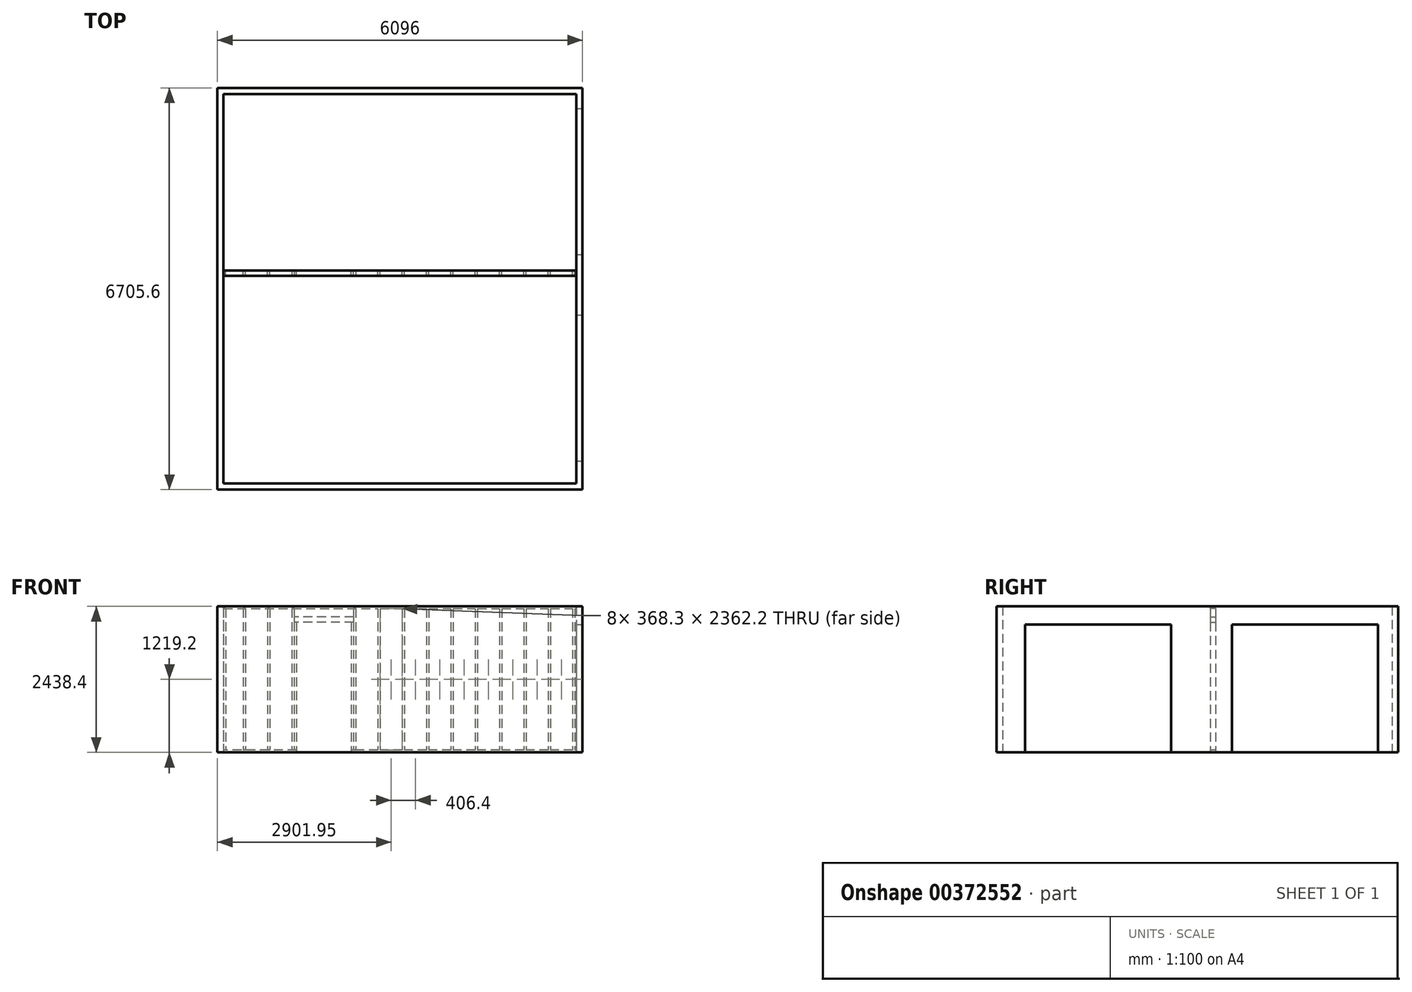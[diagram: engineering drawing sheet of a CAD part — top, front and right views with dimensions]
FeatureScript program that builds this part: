
annotation { "Feature Type Name" : "Feature", "Feature Type Description" : "" }
export const myFeature = defineFeature(function(context is Context, id is Id, definition is map)
    precondition{}
    {
        {
            var Q0;
            Q0=qCreatedBy(makeId("Top.planeOp"),FACE);
            var sketch = newSketch(context, id + "F0", { "sketchPlane" : qUnion([Q0])});
            skLineSegment(sketch, "E0.bottom", {"start": v(-222.03, 6557.87) * mm, "end": v(5873.97, 6557.87) * mm});
            skLineSegment(sketch, "E0.top", {"start": v(-222.03, -147.73) * mm, "end": v(5873.97, -147.73) * mm});
            skLineSegment(sketch, "E0.left", {"start": v(-222.03, 6557.87) * mm, "end": v(-222.03, -147.73) * mm});
            skLineSegment(sketch, "E0.right", {"start": v(5873.97, 6557.87) * mm, "end": v(5873.97, -147.73) * mm});
            skLineSegment(sketch, "E1.bottom", {"start": v(-120.43, 6456.27) * mm, "end": v(5772.37, 6456.27) * mm});
            skLineSegment(sketch, "E1.top", {"start": v(-120.43, -46.13) * mm, "end": v(5772.37, -46.13) * mm});
            skLineSegment(sketch, "E1.left", {"start": v(-120.43, 6456.27) * mm, "end": v(-120.43, -46.13) * mm});
            skLineSegment(sketch, "E1.right", {"start": v(5772.37, 6456.27) * mm, "end": v(5772.37, -46.13) * mm});
            skSolve(sketch);
        }
        {
            var Q0;
            Q0=makeQuery(id+"F0.imprint","IMPRINT",FACE,{"disambiguationData":[TD([[makeQuery(id+"F0.imprint","IMPRINT",EDGE,{"derivedFrom":sQuery(id+"F0.wireOp",EDGE,"E0.bottom")}),-1.0]])]});
            extrude(context, id + "F1", {"entities" : qUnion([Q0]), "depth" : 2438.4 * mm});
        }
        {
            var Q0;
            Q0=makeQuery(id+"F1.opExtrude","SWEPT_FACE",FACE,{"disambiguationData":[OSD([sQuery(id+"F0.wireOp",EDGE,"E0.right")])]});
            var sketch = newSketch(context, id + "F2", { "sketchPlane" : qUnion([Q0])});
            skLineSegment(sketch, "E2.bottom", {"start": v(3778.17, 0) * mm, "end": v(6216.57, 0) * mm});
            skLineSegment(sketch, "E2.top", {"start": v(3778.17, 2133.6) * mm, "end": v(6216.57, 2133.6) * mm});
            skLineSegment(sketch, "E2.left", {"start": v(3778.17, 0) * mm, "end": v(3778.17, 2133.6) * mm});
            skLineSegment(sketch, "E2.right", {"start": v(6216.57, 0) * mm, "end": v(6216.57, 2133.6) * mm});
            skLineSegment(sketch, "E3.bottom", {"start": v(326.33, 0) * mm, "end": v(2764.73, 0) * mm});
            skLineSegment(sketch, "E3.top", {"start": v(326.33, 2133.6) * mm, "end": v(2764.73, 2133.6) * mm});
            skLineSegment(sketch, "E3.left", {"start": v(326.33, 0) * mm, "end": v(326.33, 2133.6) * mm});
            skLineSegment(sketch, "E3.right", {"start": v(2764.73, 0) * mm, "end": v(2764.73, 2133.6) * mm});
            skSolve(sketch);
        }
        {
            var Q0;
            Q0 = qSketchRegion(id + "F2", true);
            var Q1;
            Q1=makeQuery(id+"F1.opExtrude","SWEPT_FACE",FACE,{"disambiguationData":[OSD([sQuery(id+"F0.wireOp",EDGE,"E1.right")])]});
            extrude(context, id + "F3", {"entities" : qUnion([Q0]), "operationType" : NewBodyOperationType.REMOVE, "endBound" : BoundingType.UP_TO_SURFACE, "oppositeDirection" : true, "endBoundEntityFace" : qUnion([Q1]), "depth" : 25.4 * mm});
        }
        {
            var Q0;
            Q0=makeQuery(id+"F1.opExtrude","CAP_FACE",FACE,{"disambiguationData":[OSD([sQuery(id+"F0.wireOp",EDGE,"E0.bottom"),sQuery(id+"F0.wireOp",EDGE,"E0.top"),sQuery(id+"F0.wireOp",EDGE,"E0.left"),sQuery(id+"F0.wireOp",EDGE,"E0.right"),sQuery(id+"F0.wireOp",EDGE,"E1.bottom"),sQuery(id+"F0.wireOp",EDGE,"E1.top"),sQuery(id+"F0.wireOp",EDGE,"E1.left"),sQuery(id+"F0.wireOp",EDGE,"E1.right")])],"isStart":false});
            var sketch = newSketch(context, id + "F4", { "sketchPlane" : qUnion([Q0])});
            skLineSegment(sketch, "E4.bottom", {"start": v(-120.43, 3420.97) * mm, "end": v(5772.37, 3420.97) * mm});
            skLineSegment(sketch, "E4.top", {"start": v(-120.43, 3509.87) * mm, "end": v(5772.37, 3509.87) * mm});
            skLineSegment(sketch, "E4.left", {"start": v(-120.43, 3420.97) * mm, "end": v(-120.43, 3509.87) * mm});
            skLineSegment(sketch, "E4.right", {"start": v(5772.37, 3420.97) * mm, "end": v(5772.37, 3509.87) * mm});
            skSolve(sketch);
        }
        {
            var Q0;
            Q0=makeQuery(id+"F4.imprint","IMPRINT",FACE,{"disambiguationData":[TD([[makeQuery(id+"F4.imprint","IMPRINT",EDGE,{"derivedFrom":sQuery(id+"F4.wireOp",EDGE,"E4.bottom")}),1.0]])]});
            extrude(context, id + "F5", {"entities" : qUnion([Q0]), "oppositeDirection" : true, "depth" : 38.1 * mm});
        }
        {
            var Q0;
            Q0=makeQuery(id+"F1.opExtrude","CAP_FACE",FACE,{"disambiguationData":[OSD([sQuery(id+"F0.wireOp",EDGE,"E0.bottom"),sQuery(id+"F0.wireOp",EDGE,"E0.top"),sQuery(id+"F0.wireOp",EDGE,"E0.left"),sQuery(id+"F0.wireOp",EDGE,"E0.right"),sQuery(id+"F0.wireOp",EDGE,"E1.bottom"),sQuery(id+"F0.wireOp",EDGE,"E1.top"),sQuery(id+"F0.wireOp",EDGE,"E1.left"),sQuery(id+"F0.wireOp",EDGE,"E1.right")])],"isStart":true});
            var sketch = newSketch(context, id + "F6", { "sketchPlane" : qUnion([Q0])});
            skLineSegment(sketch, "E5.bottom", {"start": v(5772.37, -3420.97) * mm, "end": v(-120.43, -3420.97) * mm});
            skLineSegment(sketch, "E5.top", {"start": v(5772.37, -3509.87) * mm, "end": v(-120.43, -3509.87) * mm});
            skLineSegment(sketch, "E5.left", {"start": v(5772.37, -3420.97) * mm, "end": v(5772.37, -3509.87) * mm});
            skLineSegment(sketch, "E5.right", {"start": v(-120.43, -3420.97) * mm, "end": v(-120.43, -3509.87) * mm});
            skSolve(sketch);
        }
        {
            var Q0;
            Q0=makeQuery(id+"F6.imprint","IMPRINT",FACE,{"disambiguationData":[TD([[makeQuery(id+"F6.imprint","IMPRINT",EDGE,{"derivedFrom":sQuery(id+"F6.wireOp",EDGE,"E5.bottom")}),1.0]])]});
            extrude(context, id + "F7", {"entities" : qUnion([Q0]), "oppositeDirection" : true, "depth" : 38.1 * mm});
        }
        {
            var Q0;
            Q0=makeQuery(id+"F7.opExtrude","CAP_FACE",FACE,{"disambiguationData":[OSD([sQuery(id+"F6.wireOp",EDGE,"E5.bottom"),sQuery(id+"F6.wireOp",EDGE,"E5.top"),sQuery(id+"F6.wireOp",EDGE,"E5.left"),sQuery(id+"F6.wireOp",EDGE,"E5.right")])],"isStart":true});
            var sketch = newSketch(context, id + "F8", { "sketchPlane" : qUnion([Q0])});
            skLineSegment(sketch, "E6.bottom", {"start": v(2013.17, -3509.87) * mm, "end": v(1098.77, -3509.87) * mm});
            skLineSegment(sketch, "E6.top", {"start": v(2013.17, -3420.97) * mm, "end": v(1098.77, -3420.97) * mm});
            skLineSegment(sketch, "E6.left", {"start": v(2013.17, -3509.87) * mm, "end": v(2013.17, -3420.97) * mm});
            skLineSegment(sketch, "E6.right", {"start": v(1098.77, -3509.87) * mm, "end": v(1098.77, -3420.97) * mm});
            skSolve(sketch);
        }
        {
            var Q0;
            Q0=makeQuery(id+"F8.imprint","IMPRINT",FACE,{"disambiguationData":[TD([[makeQuery(id+"F8.imprint","IMPRINT",EDGE,{"derivedFrom":sQuery(id+"F8.wireOp",EDGE,"E6.bottom")}),-1.0]])]});
            extrude(context, id + "F9", {"entities" : qUnion([Q0]), "operationType" : NewBodyOperationType.REMOVE, "endBound" : BoundingType.UP_TO_NEXT, "oppositeDirection" : true, "depth" : 25.4 * mm});
        }
        {
            var Q0;
            {var subQ0=sQuery(id+"F6.wireOp",EDGE,"E5.bottom");var subQ1=sQuery(id+"F6.wireOp",EDGE,"E5.top");var subQ2=sQuery(id+"F6.wireOp",EDGE,"E5.left");Q0=makeQuery(id+"F9.boolean.opBoolean","SPLIT",FACE,{"disambiguationData":[TD([makeQuery(id+"F7.opExtrude","SWEPT_FACE",FACE,{"disambiguationData":[OSD([subQ2])]})])],"derivedFrom":makeQuery(id+"F7.opExtrude","CAP_FACE",FACE,{"disambiguationData":[OSD([subQ0,subQ1,subQ2,sQuery(id+"F6.wireOp",EDGE,"E5.right")])],"isStart":false})});}
            var sketch = newSketch(context, id + "F10", { "sketchPlane" : qUnion([Q0])});
            skLineSegment(sketch, "E7.bottom", {"start": v(2013.17, 3420.97) * mm, "end": v(2051.27, 3420.97) * mm});
            skLineSegment(sketch, "E7.top", {"start": v(2013.17, 3509.87) * mm, "end": v(2051.27, 3509.87) * mm});
            skLineSegment(sketch, "E7.left", {"start": v(2013.17, 3420.97) * mm, "end": v(2013.17, 3509.87) * mm});
            skLineSegment(sketch, "E7.right", {"start": v(2051.27, 3420.97) * mm, "end": v(2051.27, 3509.87) * mm});
            skLineSegment(sketch, "E8.bottom", {"start": v(1098.77, 3420.97) * mm, "end": v(1060.67, 3420.97) * mm});
            skLineSegment(sketch, "E8.top", {"start": v(1098.77, 3509.87) * mm, "end": v(1060.67, 3509.87) * mm});
            skLineSegment(sketch, "E8.left", {"start": v(1098.77, 3420.97) * mm, "end": v(1098.77, 3509.87) * mm});
            skLineSegment(sketch, "E8.right", {"start": v(1060.67, 3420.97) * mm, "end": v(1060.67, 3509.87) * mm});
            skSolve(sketch);
        }
        {
            var Q0;
            Q0=makeQuery(id+"F10.imprint","IMPRINT",FACE,{"disambiguationData":[TD([[makeQuery(id+"F10.imprint","IMPRINT",EDGE,{"derivedFrom":sQuery(id+"F10.wireOp",EDGE,"E7.bottom")}),-1.0]])]});
            var Q1;
            Q1=makeQuery(id+"F10.imprint","IMPRINT",FACE,{"disambiguationData":[TD([[makeQuery(id+"F10.imprint","IMPRINT",EDGE,{"derivedFrom":sQuery(id+"F10.wireOp",EDGE,"E8.bottom")}),-1.0]])]});
            extrude(context, id + "F11", {"entities" : qUnion([Q0, Q1]), "depth" : 2133.6 * mm});
        }
        {
            var Q0;
            {var subQ0=sQuery(id+"F6.wireOp",EDGE,"E5.bottom");var subQ1=sQuery(id+"F6.wireOp",EDGE,"E5.top");var subQ2=sQuery(id+"F6.wireOp",EDGE,"E5.left");Q0=makeQuery(id+"F9.boolean.opBoolean","SPLIT",FACE,{"disambiguationData":[TD([makeQuery(id+"F7.opExtrude","SWEPT_FACE",FACE,{"disambiguationData":[OSD([subQ2])]})])],"derivedFrom":makeQuery(id+"F7.opExtrude","CAP_FACE",FACE,{"disambiguationData":[OSD([subQ0,subQ1,subQ2,sQuery(id+"F6.wireOp",EDGE,"E5.right")])],"isStart":false})});}
            var sketch = newSketch(context, id + "F12", { "sketchPlane" : qUnion([Q0])});
            skLineSegment(sketch, "E9.bottom", {"start": v(2051.27, 3509.87) * mm, "end": v(2089.37, 3509.87) * mm});
            skLineSegment(sketch, "E9.top", {"start": v(2051.27, 3420.97) * mm, "end": v(2089.37, 3420.97) * mm});
            skLineSegment(sketch, "E9.left", {"start": v(2051.27, 3509.87) * mm, "end": v(2051.27, 3420.97) * mm});
            skLineSegment(sketch, "E9.right", {"start": v(2089.37, 3509.87) * mm, "end": v(2089.37, 3420.97) * mm});
            skLineSegment(sketch, "E10.bottom", {"start": v(1060.67, 3509.87) * mm, "end": v(1022.57, 3509.87) * mm});
            skLineSegment(sketch, "E10.top", {"start": v(1060.67, 3420.97) * mm, "end": v(1022.57, 3420.97) * mm});
            skLineSegment(sketch, "E10.left", {"start": v(1060.67, 3509.87) * mm, "end": v(1060.67, 3420.97) * mm});
            skLineSegment(sketch, "E10.right", {"start": v(1022.57, 3509.87) * mm, "end": v(1022.57, 3420.97) * mm});
            skSolve(sketch);
        }
        {
            var Q0;
            Q0=makeQuery(id+"F12.imprint","IMPRINT",FACE,{"disambiguationData":[TD([[makeQuery(id+"F12.imprint","IMPRINT",EDGE,{"derivedFrom":sQuery(id+"F12.wireOp",EDGE,"E9.bottom")}),1.0]])]});
            var Q1;
            Q1=makeQuery(id+"F12.imprint","IMPRINT",FACE,{"disambiguationData":[TD([[makeQuery(id+"F12.imprint","IMPRINT",EDGE,{"derivedFrom":sQuery(id+"F12.wireOp",EDGE,"E10.bottom")}),1.0]])]});
            extrude(context, id + "F13", {"entities" : qUnion([Q0, Q1]), "depth" : 2362.2 * mm});
        }
        {
            var Q0;
            Q0=makeQuery(id+"F13.opExtrude","SWEPT_FACE",FACE,{"disambiguationData":[OSD([sQuery(id+"F12.wireOp",EDGE,"E10.left")])]});
            var sketch = newSketch(context, id + "F14", { "sketchPlane" : qUnion([Q0])});
            skLineSegment(sketch, "E11.bottom", {"start": v(3420.97, 2263.37) * mm, "end": v(3509.87, 2263.37) * mm});
            skLineSegment(sketch, "E11.top", {"start": v(3420.97, 2174.47) * mm, "end": v(3509.87, 2174.47) * mm});
            skLineSegment(sketch, "E11.left", {"start": v(3420.97, 2263.37) * mm, "end": v(3420.97, 2174.47) * mm});
            skLineSegment(sketch, "E11.right", {"start": v(3509.87, 2263.37) * mm, "end": v(3509.87, 2174.47) * mm});
            skSolve(sketch);
        }
        {
            var Q0;
            Q0=makeQuery(id+"F14.imprint","IMPRINT",FACE,{"disambiguationData":[TD([[makeQuery(id+"F14.imprint","IMPRINT",EDGE,{"derivedFrom":sQuery(id+"F14.wireOp",EDGE,"E11.bottom")}),-1.0]])]});
            extrude(context, id + "F15", {"entities" : qUnion([Q0]), "endBound" : BoundingType.UP_TO_NEXT, "depth" : 25.4 * mm});
        }
        {
            var Q0;
            {var subQ0=sQuery(id+"F6.wireOp",EDGE,"E5.bottom");var subQ1=sQuery(id+"F6.wireOp",EDGE,"E5.top");var subQ2=sQuery(id+"F6.wireOp",EDGE,"E5.left");Q0=makeQuery(id+"F9.boolean.opBoolean","SPLIT",FACE,{"disambiguationData":[TD([makeQuery(id+"F7.opExtrude","SWEPT_FACE",FACE,{"disambiguationData":[OSD([subQ2])]})])],"derivedFrom":makeQuery(id+"F7.opExtrude","CAP_FACE",FACE,{"disambiguationData":[OSD([subQ0,subQ1,subQ2,sQuery(id+"F6.wireOp",EDGE,"E5.right")])],"isStart":false})});}
            var sketch = newSketch(context, id + "F16", { "sketchPlane" : qUnion([Q0])});
            skLineSegment(sketch, "E12.bottom", {"start": v(2457.67, 3420.97) * mm, "end": v(2495.77, 3420.97) * mm});
            skLineSegment(sketch, "E12.top", {"start": v(2457.67, 3509.87) * mm, "end": v(2495.77, 3509.87) * mm});
            skLineSegment(sketch, "E12.left", {"start": v(2457.67, 3420.97) * mm, "end": v(2457.67, 3509.87) * mm});
            skLineSegment(sketch, "E12.right", {"start": v(2495.77, 3420.97) * mm, "end": v(2495.77, 3509.87) * mm});
            skLineSegment(sketch, "E13.1.0.0", {"start": v(2902.17, 3420.97) * mm, "end": v(2902.17, 3509.87) * mm});
            skLineSegment(sketch, "E13.1.0.1", {"start": v(2864.07, 3420.97) * mm, "end": v(2864.07, 3509.87) * mm});
            skLineSegment(sketch, "E13.1.0.2", {"start": v(2864.07, 3509.87) * mm, "end": v(2902.17, 3509.87) * mm});
            skLineSegment(sketch, "E13.1.0.3", {"start": v(2864.07, 3420.97) * mm, "end": v(2902.17, 3420.97) * mm});
            skLineSegment(sketch, "E13.2.0.0", {"start": v(3308.57, 3420.97) * mm, "end": v(3308.57, 3509.87) * mm});
            skLineSegment(sketch, "E13.2.0.1", {"start": v(3270.47, 3420.97) * mm, "end": v(3270.47, 3509.87) * mm});
            skLineSegment(sketch, "E13.2.0.2", {"start": v(3270.47, 3509.87) * mm, "end": v(3308.57, 3509.87) * mm});
            skLineSegment(sketch, "E13.2.0.3", {"start": v(3270.47, 3420.97) * mm, "end": v(3308.57, 3420.97) * mm});
            skLineSegment(sketch, "E13.3.0.0", {"start": v(3714.97, 3420.97) * mm, "end": v(3714.97, 3509.87) * mm});
            skLineSegment(sketch, "E13.3.0.1", {"start": v(3676.87, 3420.97) * mm, "end": v(3676.87, 3509.87) * mm});
            skLineSegment(sketch, "E13.3.0.2", {"start": v(3676.87, 3509.87) * mm, "end": v(3714.97, 3509.87) * mm});
            skLineSegment(sketch, "E13.3.0.3", {"start": v(3676.87, 3420.97) * mm, "end": v(3714.97, 3420.97) * mm});
            skLineSegment(sketch, "E13.4.0.0", {"start": v(4121.37, 3420.97) * mm, "end": v(4121.37, 3509.87) * mm});
            skLineSegment(sketch, "E13.4.0.1", {"start": v(4083.27, 3420.97) * mm, "end": v(4083.27, 3509.87) * mm});
            skLineSegment(sketch, "E13.4.0.2", {"start": v(4083.27, 3509.87) * mm, "end": v(4121.37, 3509.87) * mm});
            skLineSegment(sketch, "E13.4.0.3", {"start": v(4083.27, 3420.97) * mm, "end": v(4121.37, 3420.97) * mm});
            skLineSegment(sketch, "E13.5.0.0", {"start": v(4527.77, 3420.97) * mm, "end": v(4527.77, 3509.87) * mm});
            skLineSegment(sketch, "E13.5.0.1", {"start": v(4489.67, 3420.97) * mm, "end": v(4489.67, 3509.87) * mm});
            skLineSegment(sketch, "E13.5.0.2", {"start": v(4489.67, 3509.87) * mm, "end": v(4527.77, 3509.87) * mm});
            skLineSegment(sketch, "E13.5.0.3", {"start": v(4489.67, 3420.97) * mm, "end": v(4527.77, 3420.97) * mm});
            skLineSegment(sketch, "E13.6.0.0", {"start": v(4934.17, 3420.97) * mm, "end": v(4934.17, 3509.87) * mm});
            skLineSegment(sketch, "E13.6.0.1", {"start": v(4896.07, 3420.97) * mm, "end": v(4896.07, 3509.87) * mm});
            skLineSegment(sketch, "E13.6.0.2", {"start": v(4896.07, 3509.87) * mm, "end": v(4934.17, 3509.87) * mm});
            skLineSegment(sketch, "E13.6.0.3", {"start": v(4896.07, 3420.97) * mm, "end": v(4934.17, 3420.97) * mm});
            skLineSegment(sketch, "E13.7.0.0", {"start": v(5340.57, 3420.97) * mm, "end": v(5340.57, 3509.87) * mm});
            skLineSegment(sketch, "E13.7.0.1", {"start": v(5302.47, 3420.97) * mm, "end": v(5302.47, 3509.87) * mm});
            skLineSegment(sketch, "E13.7.0.2", {"start": v(5302.47, 3509.87) * mm, "end": v(5340.57, 3509.87) * mm});
            skLineSegment(sketch, "E13.7.0.3", {"start": v(5302.47, 3420.97) * mm, "end": v(5340.57, 3420.97) * mm});
            skLineSegment(sketch, "E13.8.0.0", {"start": v(5746.97, 3420.97) * mm, "end": v(5746.97, 3509.87) * mm});
            skLineSegment(sketch, "E13.8.0.1", {"start": v(5708.87, 3420.97) * mm, "end": v(5708.87, 3509.87) * mm});
            skLineSegment(sketch, "E13.8.0.2", {"start": v(5708.87, 3509.87) * mm, "end": v(5746.97, 3509.87) * mm});
            skLineSegment(sketch, "E13.8.0.3", {"start": v(5708.87, 3420.97) * mm, "end": v(5746.97, 3420.97) * mm});
            skLineSegment(sketch, "E13.direction1", {"start": v(2457.67, 3420.97) * mm, "end": v(2864.07, 3420.97) * mm, "construction": true});
            skSolve(sketch);
        }
        {
            var Q0;
            Q0 = qSketchRegion(id + "F16", true);
            extrude(context, id + "F17", {"entities" : qUnion([Q0]), "operationType" : NewBodyOperationType.ADD, "endBound" : BoundingType.UP_TO_NEXT, "depth" : 25.4 * mm});
        }
        {
            var Q0;
            {var subQ0=sQuery(id+"F6.wireOp",EDGE,"E5.bottom");var subQ1=sQuery(id+"F6.wireOp",EDGE,"E5.right");var subQ2=sQuery(id+"F6.wireOp",EDGE,"E5.top");Q0=makeQuery(id+"F9.boolean.opBoolean","SPLIT",FACE,{"disambiguationData":[TD([makeQuery(id+"F7.opExtrude","SWEPT_FACE",FACE,{"disambiguationData":[OSD([subQ1])]})])],"derivedFrom":makeQuery(id+"F7.opExtrude","CAP_FACE",FACE,{"disambiguationData":[OSD([subQ0,subQ2,sQuery(id+"F6.wireOp",EDGE,"E5.left"),subQ1])],"isStart":false})});}
            var sketch = newSketch(context, id + "F18", { "sketchPlane" : qUnion([Q0])});
            skLineSegment(sketch, "E14.bottom", {"start": v(654.27, 3420.97) * mm, "end": v(616.17, 3420.97) * mm});
            skLineSegment(sketch, "E14.top", {"start": v(654.27, 3509.87) * mm, "end": v(616.17, 3509.87) * mm});
            skLineSegment(sketch, "E14.left", {"start": v(654.27, 3420.97) * mm, "end": v(654.27, 3509.87) * mm});
            skLineSegment(sketch, "E14.right", {"start": v(616.17, 3420.97) * mm, "end": v(616.17, 3509.87) * mm});
            skLineSegment(sketch, "E15.bottom", {"start": v(247.87, 3420.97) * mm, "end": v(209.77, 3420.97) * mm});
            skLineSegment(sketch, "E15.top", {"start": v(247.87, 3509.87) * mm, "end": v(209.77, 3509.87) * mm});
            skLineSegment(sketch, "E15.left", {"start": v(247.87, 3420.97) * mm, "end": v(247.87, 3509.87) * mm});
            skLineSegment(sketch, "E15.right", {"start": v(209.77, 3420.97) * mm, "end": v(209.77, 3509.87) * mm});
            skLineSegment(sketch, "E16.bottom", {"start": v(-120.43, 3420.97) * mm, "end": v(-82.33, 3420.97) * mm});
            skLineSegment(sketch, "E16.top", {"start": v(-120.43, 3509.87) * mm, "end": v(-82.33, 3509.87) * mm});
            skLineSegment(sketch, "E16.left", {"start": v(-120.43, 3420.97) * mm, "end": v(-120.43, 3509.87) * mm});
            skLineSegment(sketch, "E16.right", {"start": v(-82.33, 3420.97) * mm, "end": v(-82.33, 3509.87) * mm});
            skSolve(sketch);
        }
        {
            var Q0;
            Q0 = qSketchRegion(id + "F18", true);
            extrude(context, id + "F19", {"entities" : qUnion([Q0]), "endBound" : BoundingType.UP_TO_NEXT, "depth" : 25.4 * mm});
        }
    });
